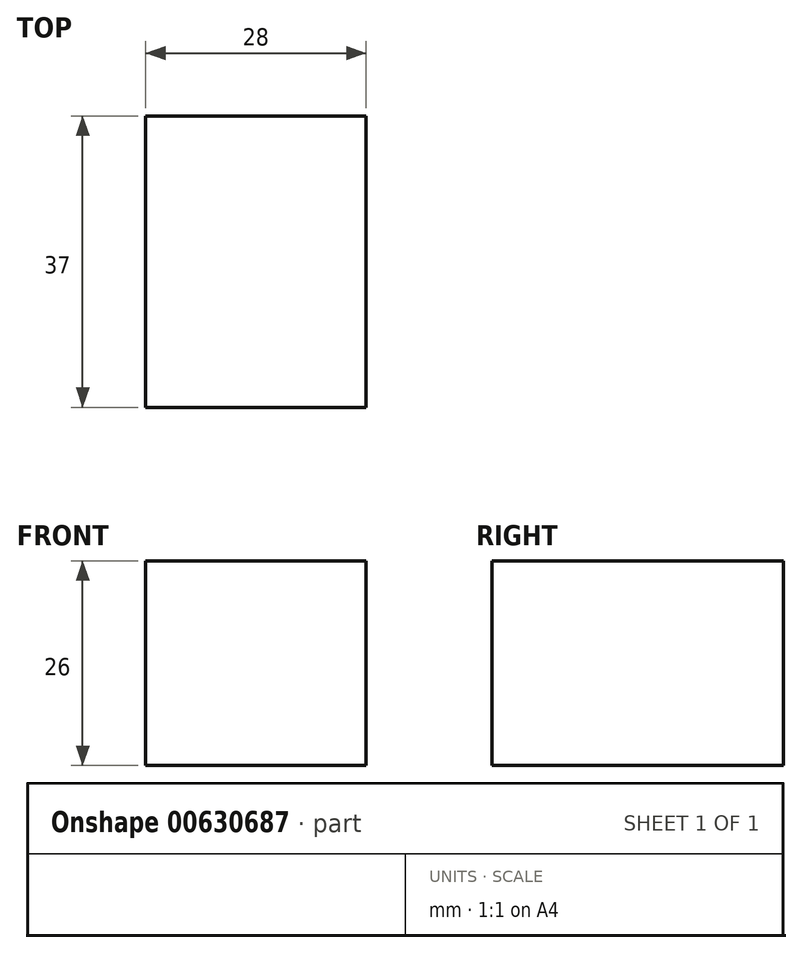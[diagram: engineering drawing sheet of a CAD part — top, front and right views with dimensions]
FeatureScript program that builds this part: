
annotation { "Feature Type Name" : "Feature", "Feature Type Description" : "" }
export const myFeature = defineFeature(function(context is Context, id is Id, definition is map)
    precondition{}
    {
        {
            var Q0;
            Q0=qCreatedBy(makeId("Front.planeOp"),FACE);
            var sketch = newSketch(context, id + "F0", { "sketchPlane" : qUnion([Q0])});
            skLineSegment(sketch, "E0.bottom", {"start": v(14, -13) * mm, "end": v(-14, -13) * mm});
            skLineSegment(sketch, "E0.top", {"start": v(14, 13) * mm, "end": v(-14, 13) * mm});
            skLineSegment(sketch, "E0.left", {"start": v(14, -13) * mm, "end": v(14, 13) * mm});
            skLineSegment(sketch, "E0.right", {"start": v(-14, -13) * mm, "end": v(-14, 13) * mm});
            skPoint(sketch, "E0.middle", {"position": v(0, 0) * mm});
            skSolve(sketch);
        }
        {
            var Q0;
            Q0 = qSketchRegion(id + "F0", true);
            extrude(context, id + "F1", {"entities" : qUnion([Q0]), "depth" : 37 * mm, "offsetDistance" : 25 * mm});
        }
    });
